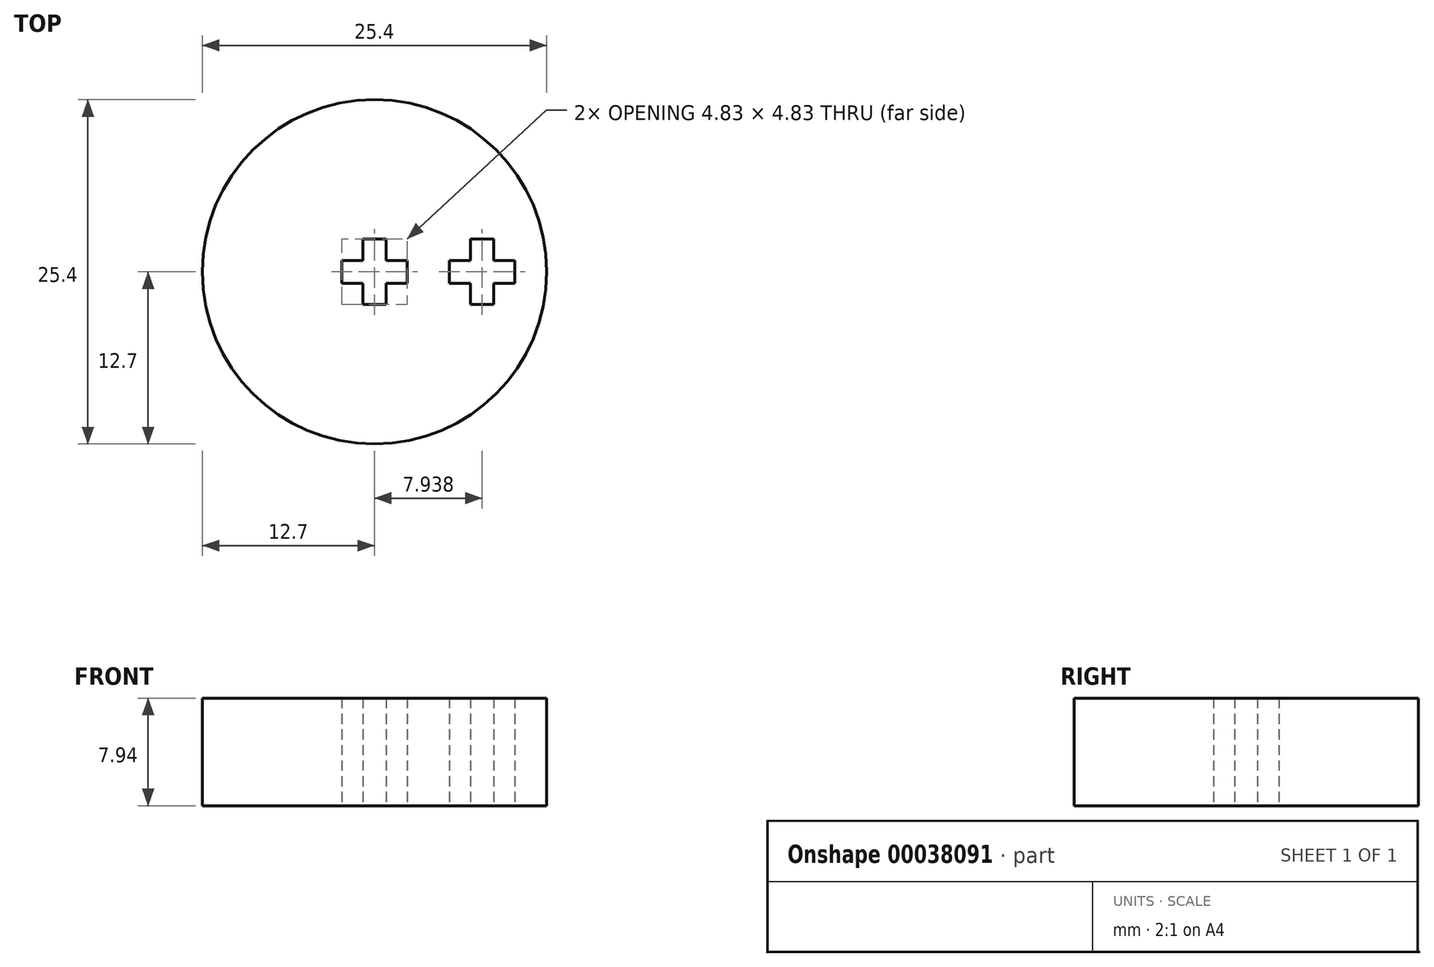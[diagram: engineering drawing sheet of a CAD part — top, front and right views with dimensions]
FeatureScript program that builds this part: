
annotation { "Feature Type Name" : "Feature", "Feature Type Description" : "" }
export const myFeature = defineFeature(function(context is Context, id is Id, definition is map)
    precondition{}
    {
        {
            var Q0;
            Q0=qCreatedBy(makeId("Top.planeOp"),FACE);
            var sketch = newSketch(context, id + "F0", { "sketchPlane" : qUnion([Q0])});
            skCircle(sketch, "E0", {"center": v(0, 0) * mm, "radius": 12.7 * mm});
            skLineSegment(sketch, "E1.rect.bottom", {"start": v(0.84, -2.41) * mm, "end": v(-0.84, -2.41) * mm});
            skLineSegment(sketch, "E1.rect.top", {"start": v(0.84, 2.41) * mm, "end": v(-0.84, 2.41) * mm});
            skLineSegment(sketch, "E1.rect.left", {"start": v(0.84, -2.41) * mm, "end": v(0.84, 2.41) * mm});
            skLineSegment(sketch, "E1.rect.right", {"start": v(-0.84, -2.41) * mm, "end": v(-0.84, 2.41) * mm});
            skLineSegment(sketch, "E2.rect.bottom", {"start": v(2.41, -0.84) * mm, "end": v(-2.41, -0.84) * mm});
            skLineSegment(sketch, "E2.rect.top", {"start": v(2.41, 0.84) * mm, "end": v(-2.41, 0.84) * mm});
            skLineSegment(sketch, "E2.rect.left", {"start": v(2.41, -0.84) * mm, "end": v(2.41, 0.84) * mm});
            skLineSegment(sketch, "E2.rect.right", {"start": v(-2.41, -0.84) * mm, "end": v(-2.41, 0.84) * mm});
            skLineSegment(sketch, "E3", {"start": v(0, 0) * mm, "end": v(7.94, 0) * mm, "construction": true});
            skLineSegment(sketch, "E4.rect.bottom", {"start": v(8.78, -2.41) * mm, "end": v(7.1, -2.41) * mm});
            skLineSegment(sketch, "E4.rect.top", {"start": v(8.78, 2.41) * mm, "end": v(7.1, 2.41) * mm});
            skLineSegment(sketch, "E4.rect.left", {"start": v(8.78, -2.41) * mm, "end": v(8.78, 2.41) * mm});
            skLineSegment(sketch, "E4.rect.right", {"start": v(7.1, -2.41) * mm, "end": v(7.1, 2.41) * mm});
            skPoint(sketch, "E4.rect.middle", {"position": v(7.94, 0) * mm});
            skLineSegment(sketch, "E5.rect.bottom", {"start": v(10.35, -0.84) * mm, "end": v(5.52, -0.84) * mm});
            skLineSegment(sketch, "E5.rect.top", {"start": v(10.35, 0.84) * mm, "end": v(5.52, 0.84) * mm});
            skLineSegment(sketch, "E5.rect.left", {"start": v(10.35, -0.84) * mm, "end": v(10.35, 0.84) * mm});
            skLineSegment(sketch, "E5.rect.right", {"start": v(5.52, -0.84) * mm, "end": v(5.52, 0.84) * mm});
            skSolve(sketch);
        }
        {
            var Q0;
            Q0 = qSketchRegion(id + "F0", true);
            extrude(context, id + "F1", {"entities" : qUnion([Q0]), "depth" : 7.94 * mm});
        }
    });
